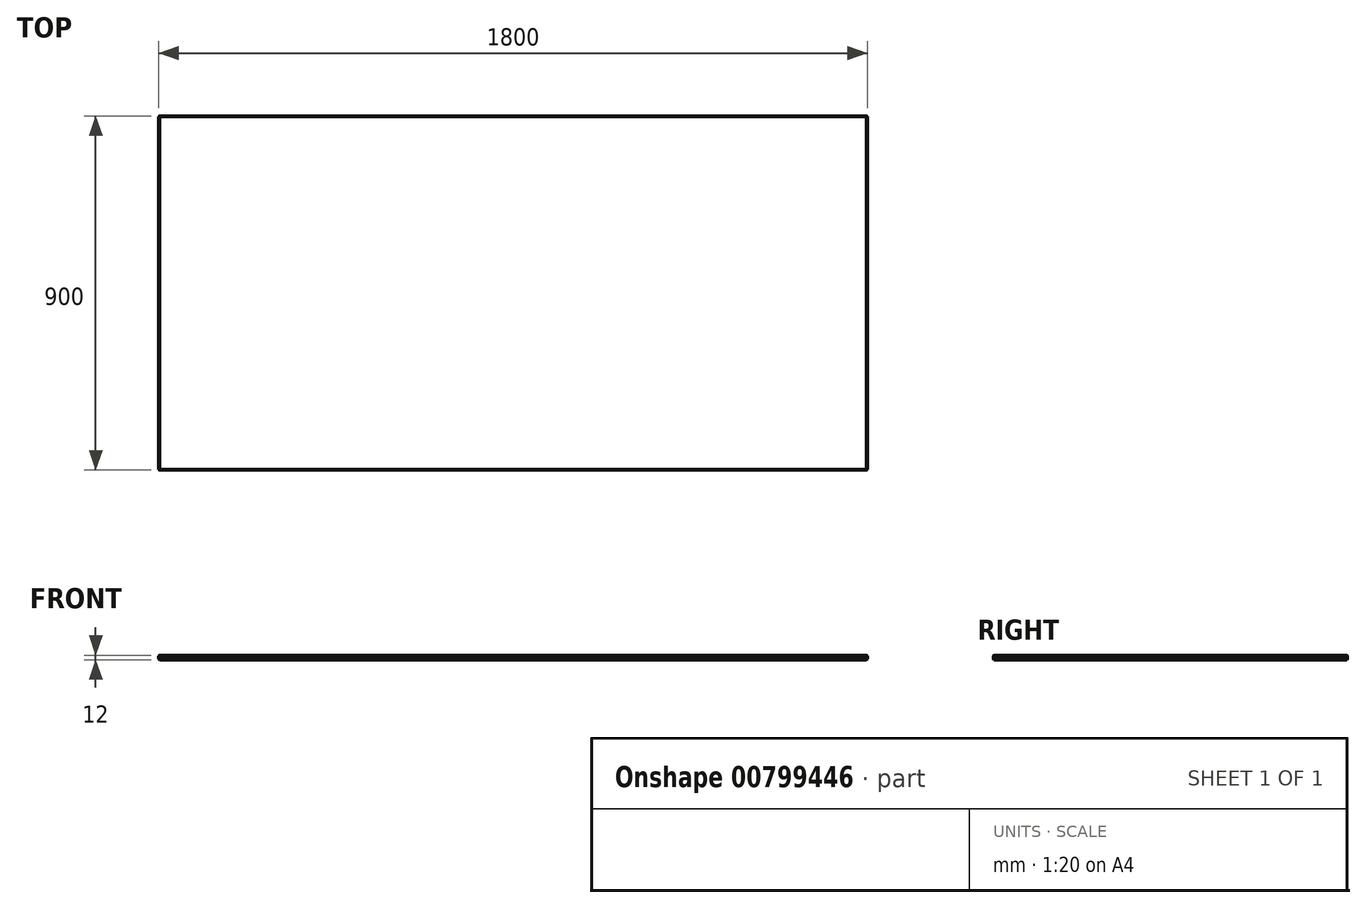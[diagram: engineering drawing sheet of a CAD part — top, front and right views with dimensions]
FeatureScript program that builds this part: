
annotation { "Feature Type Name" : "Feature", "Feature Type Description" : "" }
export const myFeature = defineFeature(function(context is Context, id is Id, definition is map)
    precondition{}
    {
        {
            var Q0;
            Q0=qCreatedBy(makeId("Top.planeOp"),FACE);
            var sketch = newSketch(context, id + "F0", { "sketchPlane" : qUnion([Q0])});
            skLineSegment(sketch, "E0.bottom", {"start": v(900, -450) * mm, "end": v(-900, -450) * mm});
            skLineSegment(sketch, "E0.top", {"start": v(900, 450) * mm, "end": v(-900, 450) * mm});
            skLineSegment(sketch, "E0.left", {"start": v(900, -450) * mm, "end": v(900, 450) * mm});
            skLineSegment(sketch, "E0.right", {"start": v(-900, -450) * mm, "end": v(-900, 450) * mm});
            skPoint(sketch, "E0.middle", {"position": v(0, 0) * mm});
            skSolve(sketch);
        }
        {
            var Q0;
            Q0=makeQuery(id+"F0.imprint","IMPRINT",FACE,{"disambiguationData":[TD([[makeQuery(id+"F0.imprint","IMPRINT",EDGE,{"derivedFrom":sQuery(id+"F0.wireOp",EDGE,"E0.bottom")}),-1.0]])]});
            extrude(context, id + "F1", {"entities" : qUnion([Q0]), "depth" : 12 * mm});
        }
        {
            var Q0;
            Q0=makeQuery(id+"F1.opExtrude","CAP_EDGE",EDGE,{"disambiguationData":[OSD([sQuery(id+"F0.wireOp",EDGE,"E0.bottom")])],"isStart":false});
            var Q1;
            Q1=makeQuery(id+"F1.opExtrude","CAP_EDGE",EDGE,{"disambiguationData":[OSD([sQuery(id+"F0.wireOp",EDGE,"E0.left")])],"isStart":true});
            var Q2;
            Q2=makeQuery(id+"F1.opExtrude","CAP_EDGE",EDGE,{"disambiguationData":[OSD([sQuery(id+"F0.wireOp",EDGE,"E0.left")])],"isStart":false});
            var Q3;
            Q3=makeQuery(id+"F1.opExtrude","CAP_EDGE",EDGE,{"disambiguationData":[OSD([sQuery(id+"F0.wireOp",EDGE,"E0.right")])],"isStart":false});
            var Q4;
            Q4=makeQuery(id+"F1.opExtrude","SWEPT_EDGE",EDGE,{"disambiguationData":[OSD([sQuery(id+"F0.wireOp",EDGE,"E0.top"),sQuery(id+"F0.wireOp",EDGE,"E0.right")])]});
            var Q5;
            Q5=makeQuery(id+"F1.opExtrude","SWEPT_EDGE",EDGE,{"disambiguationData":[OSD([sQuery(id+"F0.wireOp",EDGE,"E0.top"),sQuery(id+"F0.wireOp",EDGE,"E0.left")])]});
            var Q6;
            Q6=makeQuery(id+"F1.opExtrude","SWEPT_EDGE",EDGE,{"disambiguationData":[OSD([sQuery(id+"F0.wireOp",EDGE,"E0.bottom"),sQuery(id+"F0.wireOp",EDGE,"E0.right")])]});
            var Q7;
            Q7=makeQuery(id+"F1.opExtrude","SWEPT_EDGE",EDGE,{"disambiguationData":[OSD([sQuery(id+"F0.wireOp",EDGE,"E0.bottom"),sQuery(id+"F0.wireOp",EDGE,"E0.left")])]});
            var Q8;
            Q8=makeQuery(id+"F1.opExtrude","CAP_EDGE",EDGE,{"disambiguationData":[OSD([sQuery(id+"F0.wireOp",EDGE,"E0.bottom")])],"isStart":true});
            var Q9;
            Q9=makeQuery(id+"F1.opExtrude","CAP_EDGE",EDGE,{"disambiguationData":[OSD([sQuery(id+"F0.wireOp",EDGE,"E0.top")])],"isStart":true});
            var Q10;
            Q10=makeQuery(id+"F1.opExtrude","CAP_EDGE",EDGE,{"disambiguationData":[OSD([sQuery(id+"F0.wireOp",EDGE,"E0.top")])],"isStart":false});
            var Q11;
            Q11=makeQuery(id+"F1.opExtrude","CAP_EDGE",EDGE,{"disambiguationData":[OSD([sQuery(id+"F0.wireOp",EDGE,"E0.right")])],"isStart":true});
            chamfer(context, id + "F2", {"entities" : qUnion([Q0, Q1, Q2, Q3, Q4, Q5, Q6, Q7, Q8, Q9, Q10, Q11]), "width" : 2 * mm, "tangentPropagation" : true});
        }
    });
